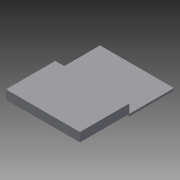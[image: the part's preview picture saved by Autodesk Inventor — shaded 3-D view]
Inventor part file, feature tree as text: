
AUTODESK INVENTOR PART (.ipt)
format: ipt  version: 2014 SP1 (Build 180222100, 222)  size: 78,848 bytes
history: native  units: in
note: dims shown in document units (in); Inventor stores cm internally (conversion verified against a paired STEP export)
features: extrude x2, sketch x2
ambient origin geometry x8: Origin, YZ Plane, XZ Plane, XY Plane, X Axis, Y Axis, Z Axis, Center Point
bodies: Solid1 (feature_tree)
feature tree (4):
  extrude  "Extrusion1"  Depth=4.0in
  extrude  "Extrusion3"  Depth=33.0in
  sketch  "Sketch1"  dims[d0=33.0in d1=4.0in]
  sketch  "Sketch3"  dims[d2=22.0in d3=0.0in d8=33.0in d9=1.0in d10=20.0in d11=0.0in]
